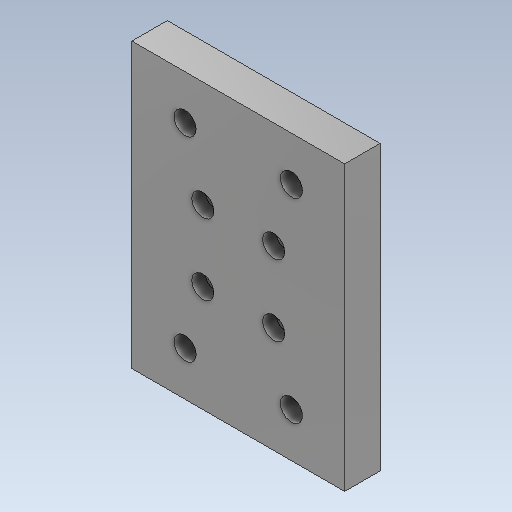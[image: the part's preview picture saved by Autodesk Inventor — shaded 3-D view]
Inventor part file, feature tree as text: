
AUTODESK INVENTOR PART (.ipt)
format: ipt  version: 2020 (Build 240168000, 168)  size: 262,656 bytes
history: native  units: in
note: dims shown in document units (in); Inventor stores cm internally (conversion verified against a paired STEP export)
features: reference x5, extrude x3, sketch x3, other x3
ambient origin geometry x8: Origin, YZ Plane, XZ Plane, XY Plane, X Axis, Y Axis, Z Axis, Center Point
bodies: Solid1 (feature_tree)
feature tree (14):
  extrude  "Extrusion1"  Depth=4.0in
  extrude  "Extrusion3"  Depth=0.3125in
  extrude  "Extrusion4"  Depth=0.5in TaperAngle=0.0deg
  sketch  "Sketch1"  dims[d0=3.0in d1=4.0in]
  reference  "Reference1"
  reference  "Reference2"
  reference  "Reference3"
  reference  "Reference4"
  reference  "Reference5"
  sketch  "Sketch3"  dims[d2=0.3125in d3=0.625in]
  sketch  "Sketch4"  dims[d4=0.75in d5=0.5in d6=0.0in d16=1.75in d17=1.75in d18=1.125in d19=0.625in d23=0.5in d24=0.375in d25=0.375in d26=0.7874in d28=1.0in d29=0.7874in d31=1.0in d34=0.3125in d35=0.0in d36=0.3125in d37=0.3125in d38=0.3125in d39=0.3125in d40=0.3125in d41=0.0in]
  other  "<userpath>\Desktop\PnP Machine\PnP Machine.iam"
  other  "PnP Machine.iam"
  other  "47065T605_ALUMINUM T-SLOTTED FRAMING EXTRUSION:2"
